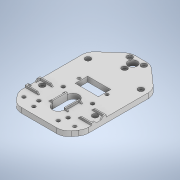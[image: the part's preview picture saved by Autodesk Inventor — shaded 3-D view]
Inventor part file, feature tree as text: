
AUTODESK INVENTOR PART (.ipt)
format: ipt  version: 2020 (Build 240168000, 168)  size: 441,344 bytes
history: native  units: mm
features: extrude x9, sketch x9, chamfer x1, plane x1, mirror x1, hole x1, fillet x1, projected_geometry x1
ambient origin geometry x8: Origin, YZ Plane, XZ Plane, XY Plane, X Axis, Y Axis, Z Axis, Center Point
bodies: Solid1 (feature_tree)
feature tree (24):
  extrude  "Extrusion1"  Depth=80.0mm
  extrude  "Extrusion2"  Depth=20.0mm
  chamfer  "Chamfer1"  Distance=5.0mm
  plane  "Work Plane1"
  extrude  "Extrusion3"  Depth=12.2mm
  mirror  "Mirror1"
  sketch  "Sketch4"  dims[d8=24.4mm d9=20.0mm]
  extrude  "Extrusion4"  Depth=20.0mm
  extrude  "Extrusion5"  Depth=5.0mm
  extrude  "Extrusion6"  Depth=2.0mm TaperAngle=45.0deg
  extrude  "Extrusion7"  Depth=10.0mm
  hole  "Hole1"  [1 undecoded]
  fillet  "Fillet1"  [1 undecoded]
  extrude  "Extrusion8"  Depth=5.0mm
  extrude  "Extrusion9"  Depth=5.0mm
  sketch  "Sketch1"  dims[d0=65.0mm d1=80.0mm]
  sketch  "Sketch2"  dims[d2=20.0mm d3=20.0mm d4=5.0mm d5=0.0mm]
  sketch  "Sketch3"  dims[d6=1.2mm d7=12.2mm]
  sketch  "Sketch5"  dims[d10=2.0mm d11=0.0mm d12=5.0mm]
  sketch  "Sketch7"  dims[d13=5.0mm d14=2.0mm d15=2.0mm d16=45.0deg]
  sketch  "Sketch8"  dims[d17=10.0mm d19=2.5mm]
  sketch  "Sketch12"  dims[d20=24.0mm d21=3.4mm d22=0.0mm d23=0.0mm]
  projected_geometry  "Projected Loop2"
  sketch  "Sketch13"  dims[d24=9.0mm d25=13.856mm d26=3.3mm d27=8.0mm d28=0.0mm d29=0.0mm d30=53.0mm d31=22.7mm d32=12.2mm d33=13.75mm d34=13.75mm d35=3.0mm d36=0.0mm d37=0.0mm d38=3.3mm d40=24.0mm d41=0.0mm d42=0.0mm d43=10.0mm d44=3.3mm d45=50.0mm d46=0.0mm d47=0.0mm d48=45.0mm d49=52.0mm d50=29.0mm d51=3.0mm d52=6.0mm d53=5.4mm d54=2.3mm d55=90.0deg d56=8.0mm d57=20.594885mm d66=9.0mm d67=9.0mm d68=12.0mm d69=12.0mm d71=12.0mm d72=3.0mm d73=9.0mm d74=11.0mm d75=10.0mm d76=10.0mm d77=20.0mm d78=6.0mm d79=5.0mm d80=5.0mm d81=0.0mm d82=0.0mm d83=0.0mm d84=0.0mm]
note: 2 required parameter values undecoded (feature->parameter linkage not recoverable at this tier; creation-order binding heuristic only, values carry confidence <= 0.55)
